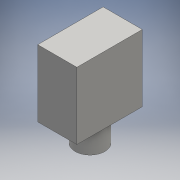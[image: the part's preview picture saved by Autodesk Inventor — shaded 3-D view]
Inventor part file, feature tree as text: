
AUTODESK INVENTOR PART (.ipt)
format: ipt  version: 2016 (Build 200138000, 138)  size: 94,720 bytes
history: native  units: mm
features: extrude x2, sketch x2
ambient origin geometry x8: Origin, YZ Plane, XZ Plane, XY Plane, X Axis, Y Axis, Z Axis, Center Point
bodies: Solid1 (feature_tree)
feature tree (4):
  extrude  "Extrusion1"  Depth=13.2mm
  extrude  "Extrusion2"  Depth=5.0mm
  sketch  "Sketch1"  dims[d0=7.9mm d1=13.2mm]
  sketch  "Sketch2"  dims[d2=13.5mm d3=0.0mm d4=6.0mm d5=5.0mm d6=0.0mm]
